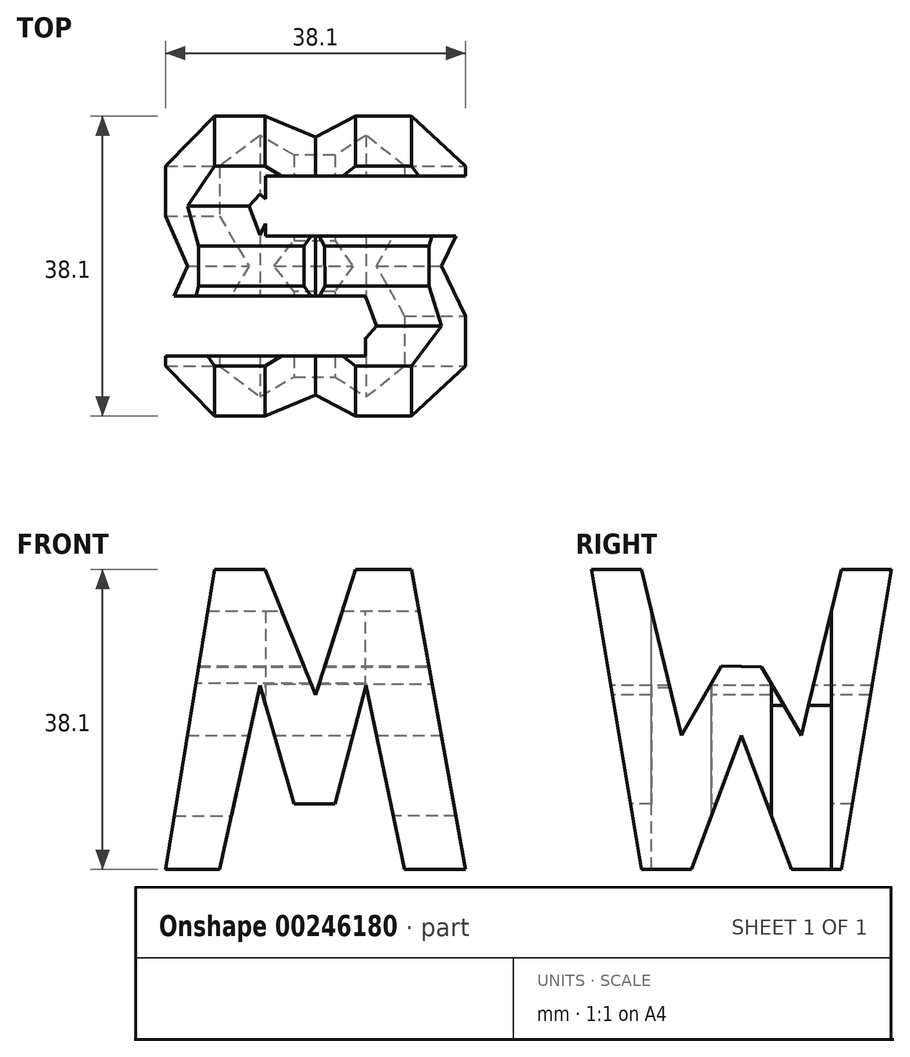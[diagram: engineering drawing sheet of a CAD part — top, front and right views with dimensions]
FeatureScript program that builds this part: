
annotation { "Feature Type Name" : "Feature", "Feature Type Description" : "" }
export const myFeature = defineFeature(function(context is Context, id is Id, definition is map)
    precondition{}
    {
        {
            var Q0;
            Q0=qCreatedBy(makeId("Front.planeOp"),FACE);
            var sketch = newSketch(context, id + "F0", { "sketchPlane" : qUnion([Q0])});
            skLineSegment(sketch, "E0", {"start": v(0, 0) * mm, "end": v(38.1, 0) * mm});
            skLineSegment(sketch, "E1", {"start": v(38.1, 0) * mm, "end": v(38.1, 38.1) * mm});
            skLineSegment(sketch, "E2", {"start": v(38.1, 38.1) * mm, "end": v(0, 38.1) * mm});
            skLineSegment(sketch, "E3", {"start": v(0, 38.1) * mm, "end": v(0, 0) * mm});
            skSolve(sketch);
        }
        {
            var Q0;
            Q0 = qSketchRegion(id + "F0", true);
            extrude(context, id + "F1", {"entities" : qUnion([Q0]), "depth" : 38.1 * mm});
        }
        {
            var Q0;
            Q0=qCreatedBy(makeId("Front.planeOp"),FACE);
            cPlane(context, id + "F2", {"entities" : qUnion([Q0]), "cplaneType" : CPlaneType.OFFSET, "offset" : 38.1 * mm, "width" : 152.4 * mm, "height" : 152.4 * mm});
        }
        {
            var Q0;
            Q0=qCreatedBy(makeId("Top.planeOp"),FACE);
            cPlane(context, id + "F3", {"entities" : qUnion([Q0]), "cplaneType" : CPlaneType.OFFSET, "offset" : 38.1 * mm, "width" : 152.4 * mm, "height" : 152.4 * mm});
        }
        {
            var Q0;
            Q0=makeQuery(id+"F1.opExtrude","SWEPT_FACE",FACE,{"disambiguationData":[OSD([sQuery(id+"F0.wireOp",EDGE,"E1")])]});
            var sketch = newSketch(context, id + "F4", { "sketchPlane" : qUnion([Q0])});
            skLineSegment(sketch, "E4", {"start": v(-38.1, 38.1) * mm, "end": v(-31.75, 0) * mm});
            skLineSegment(sketch, "E5", {"start": v(-31.75, 38.1) * mm, "end": v(-26.67, 17) * mm});
            skLineSegment(sketch, "E6", {"start": v(-25.4, 0) * mm, "end": v(-19.05, 17) * mm});
            skLineSegment(sketch, "E7", {"start": v(-19.05, 17) * mm, "end": v(-12.7, 0) * mm});
            skLineSegment(sketch, "E8", {"start": v(-6.35, 0) * mm, "end": v(0, 38.1) * mm});
            skLineSegment(sketch, "E9", {"start": v(-6.35, 38.1) * mm, "end": v(-11.43, 17) * mm});
            skLineSegment(sketch, "E10", {"start": v(-11.43, 17) * mm, "end": v(-16.51, 25.75) * mm});
            skLineSegment(sketch, "E11", {"start": v(-16.51, 25.75) * mm, "end": v(-21.6, 25.87) * mm});
            skLineSegment(sketch, "E12", {"start": v(-21.6, 25.87) * mm, "end": v(-26.67, 17) * mm});
            skLineSegment(sketch, "E13.bottom", {"start": v(0, 0) * mm, "end": v(-38.1, 0) * mm});
            skLineSegment(sketch, "E13.top", {"start": v(0, 38.1) * mm, "end": v(-38.1, 38.1) * mm});
            skLineSegment(sketch, "E13.left", {"start": v(0, 0) * mm, "end": v(0, 38.1) * mm});
            skLineSegment(sketch, "E13.right", {"start": v(-38.1, 0) * mm, "end": v(-38.1, 38.1) * mm});
            skLineSegment(sketch, "E14", {"start": v(-38.1, 38.1) * mm, "end": v(-31.75, 38.1) * mm});
            skLineSegment(sketch, "E15", {"start": v(-6.35, 38.1) * mm, "end": v(0, 38.1) * mm});
            skLineSegment(sketch, "E16", {"start": v(-6.35, 0) * mm, "end": v(-12.7, 0) * mm});
            skLineSegment(sketch, "E17", {"start": v(-25.4, 0) * mm, "end": v(-31.75, 0) * mm});
            skLineSegment(sketch, "E18", {"start": v(-31.75, 38.1) * mm, "end": v(-38.1, 38.1) * mm});
            skSolve(sketch);
        }
        {
            var Q0;
            Q0=makeQuery(id+"F4.imprint","IMPRINT",FACE,{"disambiguationData":[TD([[makeQuery(id+"F4.imprint","IMPRINT",EDGE,{"derivedFrom":sQuery(id+"F4.wireOp",EDGE,"E4")}),1.0]])]});
            var sketch = newSketch(context, id + "F5", { "sketchPlane" : qUnion([Q0])});
            skSolve(sketch);
        }
        {
            var Q0;
            Q0 = qSketchRegion(id + "F5", true);
            var Q1;
            Q1=makeQuery(id+"F4.imprint","IMPRINT",FACE,{"disambiguationData":[TD([[makeQuery(id+"F4.imprint","IMPRINT",EDGE,{"derivedFrom":sQuery(id+"F4.wireOp",EDGE,"E5")}),1.0]])]});
            var Q2;
            {var subQ0=sQuery(id+"F4.wireOp",EDGE,"E4");Q2=makeQuery(id+"F4.imprint","IMPRINT",FACE,{"disambiguationData":[TD([[makeQuery(id+"F4.imprint","IMPRINT",EDGE,{"derivedFrom":subQ0}),-1.0]])]});}
            var Q3;
            {var subQ0=sQuery(id+"F4.wireOp",EDGE,"E8");Q3=makeQuery(id+"F4.imprint","IMPRINT",FACE,{"disambiguationData":[TD([[makeQuery(id+"F4.imprint","IMPRINT",EDGE,{"derivedFrom":subQ0}),-1.0]])]});}
            var Q4;
            {var subQ0=sQuery(id+"F4.wireOp",EDGE,"E6");Q4=makeQuery(id+"F4.imprint","IMPRINT",FACE,{"disambiguationData":[TD([[makeQuery(id+"F4.imprint","IMPRINT",EDGE,{"derivedFrom":subQ0}),-1.0]])]});}
            extrude(context, id + "F6", {"entities" : qUnion([Q0, Q1, Q2, Q3, Q4]), "operationType" : NewBodyOperationType.REMOVE, "oppositeDirection" : true, "depth" : 38.1 * mm});
        }
        {
            var Q0;
            Q0=qCreatedBy(id+"F2.planeOp",FACE);
            var sketch = newSketch(context, id + "F7", { "sketchPlane" : qUnion([Q0])});
            skLineSegment(sketch, "E19", {"start": v(0, 0) * mm, "end": v(6.2, 38.1) * mm});
            skLineSegment(sketch, "E20", {"start": v(6.87, 0) * mm, "end": v(11.97, 23.37) * mm});
            skLineSegment(sketch, "E21", {"start": v(11.97, 23.37) * mm, "end": v(16.3, 8.31) * mm});
            skLineSegment(sketch, "E22", {"start": v(16.3, 8.31) * mm, "end": v(21.5, 8.31) * mm});
            skLineSegment(sketch, "E23", {"start": v(21.5, 8.31) * mm, "end": v(25.48, 23.37) * mm});
            skLineSegment(sketch, "E24", {"start": v(25.48, 23.37) * mm, "end": v(30.36, 0) * mm});
            skLineSegment(sketch, "E25", {"start": v(38.1, 0) * mm, "end": v(31.25, 38.1) * mm});
            skLineSegment(sketch, "E26", {"start": v(24.16, 38.1) * mm, "end": v(19.05, 22.17) * mm});
            skPoint(sketch, "E26.endSnap0", {"position": v(19.05, 38.1) * mm});
            skLineSegment(sketch, "E27", {"start": v(19.05, 22.17) * mm, "end": v(12.63, 38.1) * mm});
            skLineSegment(sketch, "E28.bottom", {"start": v(0, 0) * mm, "end": v(38.1, 0) * mm});
            skLineSegment(sketch, "E28.top", {"start": v(0, 38.1) * mm, "end": v(38.1, 38.1) * mm});
            skLineSegment(sketch, "E28.left", {"start": v(0, 0) * mm, "end": v(0, 38.1) * mm});
            skLineSegment(sketch, "E28.right", {"start": v(38.1, 0) * mm, "end": v(38.1, 38.1) * mm});
            skSolve(sketch);
        }
        {
            var Q0;
            {var subQ0=sQuery(id+"F7.wireOp",EDGE,"E19");Q0=makeQuery(id+"F7.imprint","IMPRINT",FACE,{"disambiguationData":[TD([[makeQuery(id+"F7.imprint","IMPRINT",EDGE,{"derivedFrom":subQ0}),1.0]])]});}
            var Q1;
            {var subQ0=sQuery(id+"F7.wireOp",EDGE,"E20");Q1=makeQuery(id+"F7.imprint","IMPRINT",FACE,{"disambiguationData":[TD([[makeQuery(id+"F7.imprint","IMPRINT",EDGE,{"derivedFrom":subQ0}),-1.0]])]});}
            var Q2;
            {var subQ0=sQuery(id+"F7.wireOp",EDGE,"E25");Q2=makeQuery(id+"F7.imprint","IMPRINT",FACE,{"disambiguationData":[TD([[makeQuery(id+"F7.imprint","IMPRINT",EDGE,{"derivedFrom":subQ0}),-1.0]])]});}
            var Q3;
            {var subQ0=sQuery(id+"F7.wireOp",EDGE,"E26");Q3=makeQuery(id+"F7.imprint","IMPRINT",FACE,{"disambiguationData":[TD([[makeQuery(id+"F7.imprint","IMPRINT",EDGE,{"derivedFrom":subQ0}),-1.0]])]});}
            extrude(context, id + "F8", {"entities" : qUnion([Q0, Q1, Q2, Q3]), "operationType" : NewBodyOperationType.REMOVE, "oppositeDirection" : true, "depth" : 38.1 * mm});
        }
        {
            var Q0;
            Q0=qCreatedBy(id+"F3.planeOp",FACE);
            var sketch = newSketch(context, id + "F9", { "sketchPlane" : qUnion([Q0])});
            skLineSegment(sketch, "E29", {"start": v(12.7, -7.62) * mm, "end": v(12.7, -15.24) * mm});
            skLineSegment(sketch, "E30", {"start": v(12.7, -15.24) * mm, "end": v(38.1, -15.24) * mm});
            skLineSegment(sketch, "E31", {"start": v(12.7, -7.62) * mm, "end": v(38.1, -7.62) * mm});
            skLineSegment(sketch, "E32", {"start": v(25.4, -30.48) * mm, "end": v(25.4, -22.86) * mm});
            skLineSegment(sketch, "E33", {"start": v(25.4, -22.86) * mm, "end": v(0, -22.86) * mm});
            skLineSegment(sketch, "E34", {"start": v(25.4, -30.48) * mm, "end": v(0, -30.48) * mm});
            skLineSegment(sketch, "E35.bottom", {"start": v(0, -38.1) * mm, "end": v(38.1, -38.1) * mm});
            skLineSegment(sketch, "E35.top", {"start": v(0, 0) * mm, "end": v(38.1, 0) * mm});
            skLineSegment(sketch, "E35.left", {"start": v(0, -38.1) * mm, "end": v(0, 0) * mm});
            skLineSegment(sketch, "E35.right", {"start": v(38.1, -38.1) * mm, "end": v(38.1, 0) * mm});
            skLineSegment(sketch, "E36", {"start": v(38.1, 0) * mm, "end": v(0, 0) * mm});
            skSolve(sketch);
        }
        {
            var Q0;
            Q0=makeQuery(id+"F9.imprint","IMPRINT",FACE,{"disambiguationData":[TD([[makeQuery(id+"F9.imprint","IMPRINT",EDGE,{"derivedFrom":sQuery(id+"F9.wireOp",EDGE,"E29")}),1.0]])]});
            var Q1;
            Q1=makeQuery(id+"F9.imprint","IMPRINT",FACE,{"disambiguationData":[TD([[makeQuery(id+"F9.imprint","IMPRINT",EDGE,{"derivedFrom":sQuery(id+"F9.wireOp",EDGE,"E32")}),1.0]])]});
            extrude(context, id + "F10", {"entities" : qUnion([Q0, Q1]), "operationType" : NewBodyOperationType.REMOVE, "oppositeDirection" : true, "depth" : 38.1 * mm});
        }
    });
